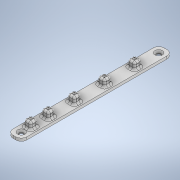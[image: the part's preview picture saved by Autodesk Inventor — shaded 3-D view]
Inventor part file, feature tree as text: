
AUTODESK INVENTOR PART (.ipt)
format: ipt  version: 2022 (Build 260153000, 153)  size: 306,176 bytes
history: native  units: mm
features: sketch x4, extrude x3, fillet x2, chamfer x1, other x1
ambient origin geometry x8: Origin, YZ Plane, XZ Plane, XY Plane, X Axis, Y Axis, Z Axis, Center Point
bodies: Solide1 (feature_tree)
feature tree (11):
  extrude  "Extrusion1"  Depth=10.0mm
  extrude  "Extrusion2"  Depth=90.0mm
  chamfer  "Chanfrein1"  Distance=10.0mm
  extrude  "Extrusion3"  Depth=10.0mm
  other  "Révolution1"
  fillet  "Congé1"  Radius=2.0mm
  fillet  "Congé2"  Radius=10.0mm
  sketch  "Esquisse1"
  sketch  "Esquisse2"
  sketch  "Esquisse3"
  sketch  "Esquisse4"
